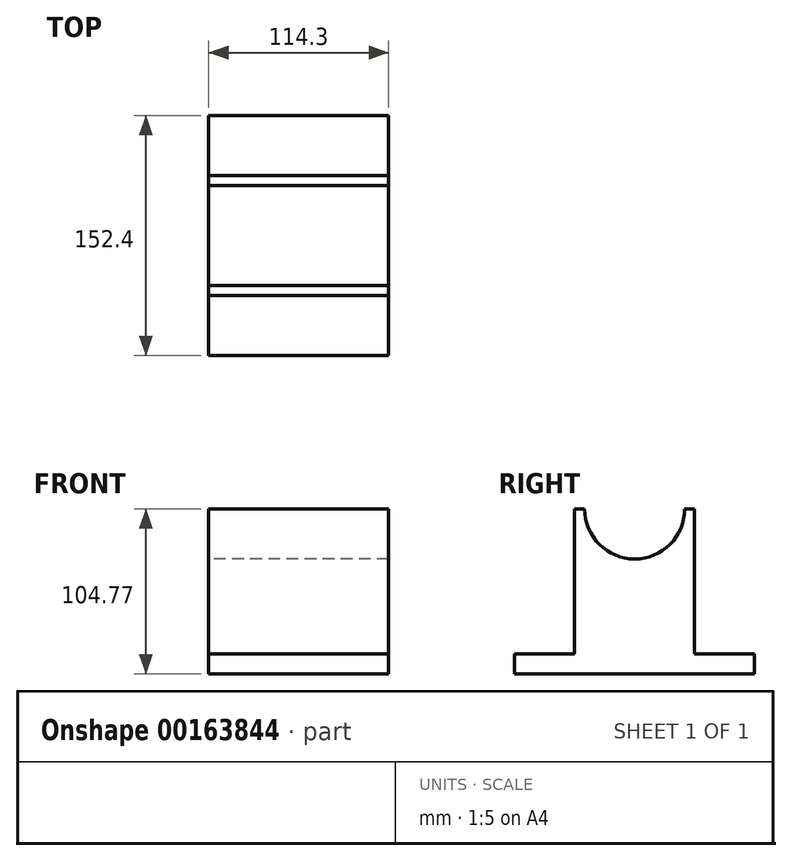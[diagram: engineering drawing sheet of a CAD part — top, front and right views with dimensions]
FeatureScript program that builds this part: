
annotation { "Feature Type Name" : "Feature", "Feature Type Description" : "" }
export const myFeature = defineFeature(function(context is Context, id is Id, definition is map)
    precondition{}
    {
        {
            var Q0;
            Q0=qCreatedBy(makeId("Right.planeOp"),FACE);
            var sketch = newSketch(context, id + "F0", { "sketchPlane" : qUnion([Q0])});
            skLineSegment(sketch, "E0", {"start": v(0, 0) * mm, "end": v(152.4, 0) * mm});
            skLineSegment(sketch, "E1", {"start": v(0, 0) * mm, "end": v(0, 12.7) * mm});
            skLineSegment(sketch, "E2", {"start": v(152.4, 0) * mm, "end": v(152.4, 12.7) * mm});
            skLineSegment(sketch, "E3", {"start": v(0, 12.7) * mm, "end": v(38.1, 12.7) * mm});
            skLineSegment(sketch, "E4", {"start": v(152.4, 12.7) * mm, "end": v(114.3, 12.7) * mm});
            skLineSegment(sketch, "E5", {"start": v(38.1, 12.7) * mm, "end": v(38.1, 104.78) * mm});
            skLineSegment(sketch, "E6", {"start": v(114.3, 12.7) * mm, "end": v(114.3, 104.78) * mm});
            skLineSegment(sketch, "E7", {"start": v(38.1, 104.78) * mm, "end": v(44.45, 104.78) * mm});
            skLineSegment(sketch, "E8", {"start": v(114.3, 104.78) * mm, "end": v(107.95, 104.78) * mm});
            skArc(sketch, "E9", {"start": v(44.45, 104.77) * mm, "mid": v(76.2, 73.03) * mm, "end": v(107.95, 104.78) * mm});
            skSolve(sketch);
        }
        {
            var Q0;
            Q0 = qSketchRegion(id + "F0", true);
            extrude(context, id + "F1", {"entities" : qUnion([Q0]), "depth" : 114.3 * mm});
        }
    });
